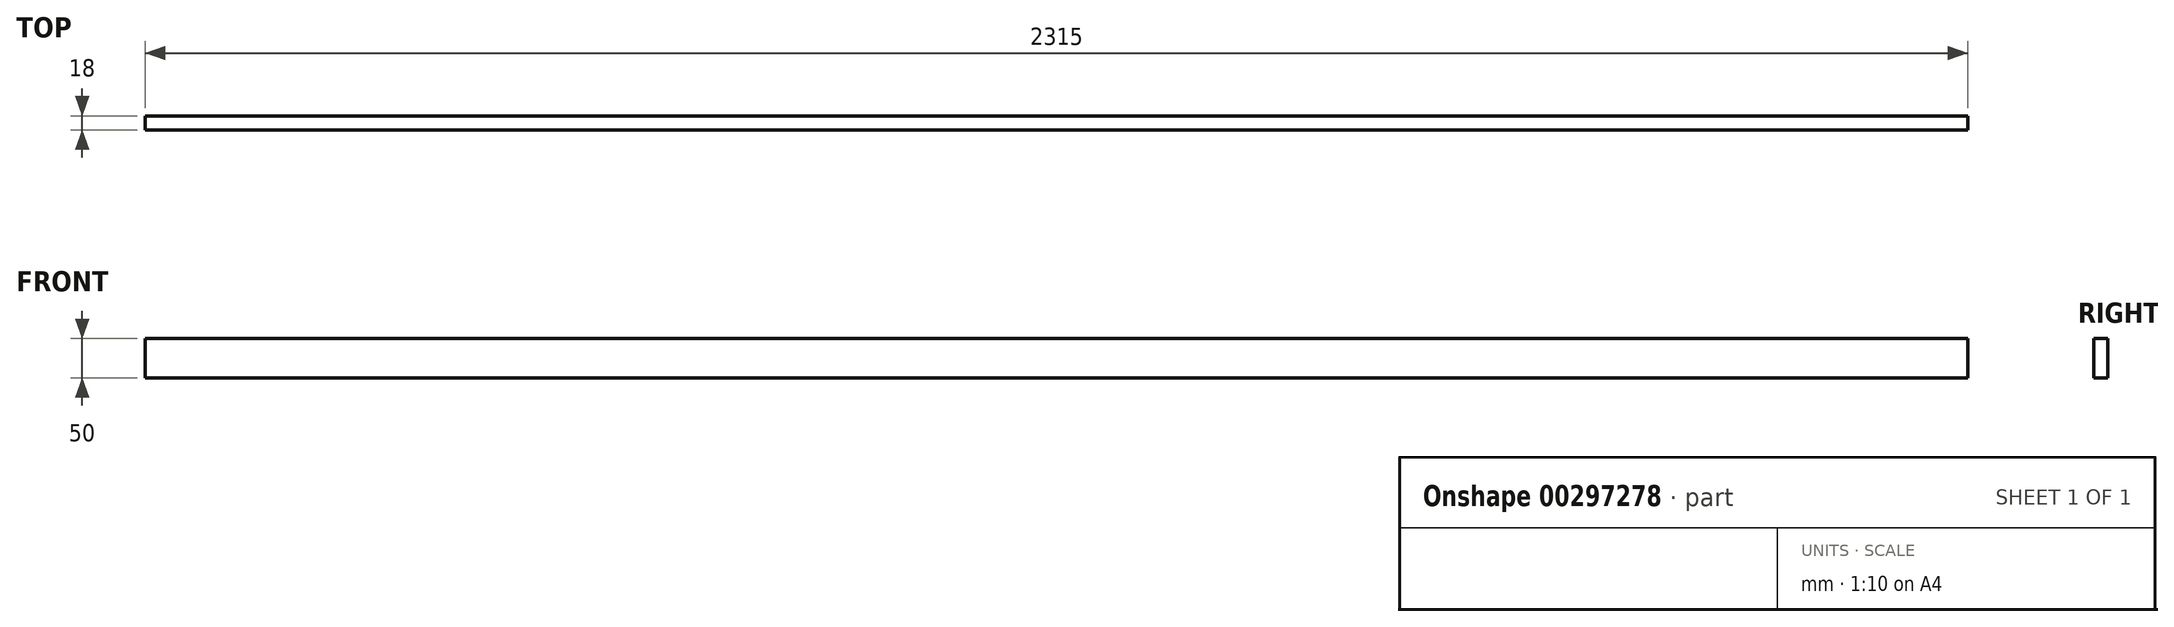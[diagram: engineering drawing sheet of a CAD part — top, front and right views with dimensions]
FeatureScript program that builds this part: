
annotation { "Feature Type Name" : "Feature", "Feature Type Description" : "" }
export const myFeature = defineFeature(function(context is Context, id is Id, definition is map)
    precondition{}
    {
        {
            var Q0;
            Q0=qCreatedBy(makeId("Right.planeOp"),FACE);
            var sketch = newSketch(context, id + "F0", { "sketchPlane" : qUnion([Q0])});
            skLineSegment(sketch, "E0.bottom", {"start": v(9, 25) * mm, "end": v(-9, 25) * mm});
            skLineSegment(sketch, "E0.top", {"start": v(9, -25) * mm, "end": v(-9, -25) * mm});
            skLineSegment(sketch, "E0.left", {"start": v(9, 25) * mm, "end": v(9, -25) * mm});
            skLineSegment(sketch, "E0.right", {"start": v(-9, 25) * mm, "end": v(-9, -25) * mm});
            skPoint(sketch, "E0.middle", {"position": v(0, 0) * mm});
            skSolve(sketch);
        }
        {
            var Q0;
            Q0 = qSketchRegion(id + "F0", true);
            extrude(context, id + "F1", {"entities" : qUnion([Q0]), "depth" : 2315 * mm});
        }
    });
